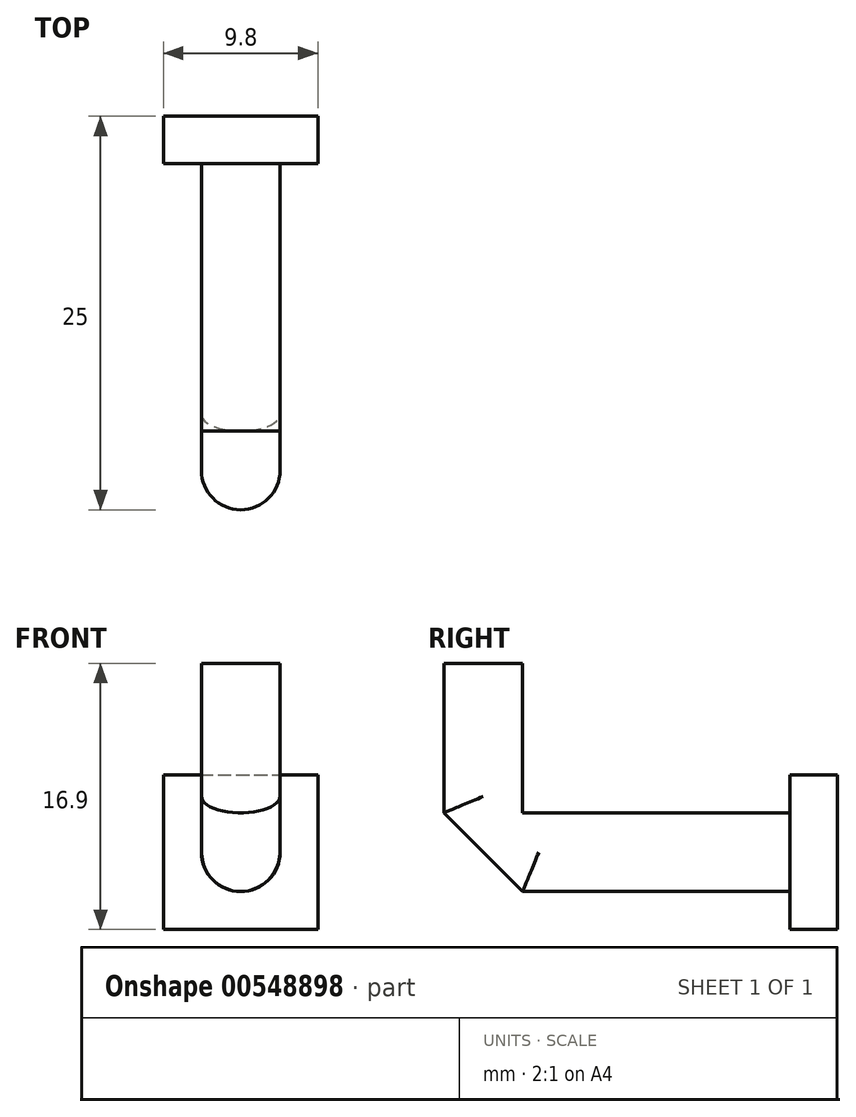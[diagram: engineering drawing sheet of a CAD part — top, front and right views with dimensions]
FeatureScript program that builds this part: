
annotation { "Feature Type Name" : "Feature", "Feature Type Description" : "" }
export const myFeature = defineFeature(function(context is Context, id is Id, definition is map)
    precondition{}
    {
        {
            var Q0;
            Q0=qCreatedBy(makeId("Front.planeOp"),FACE);
            var sketch = newSketch(context, id + "F0", { "sketchPlane" : qUnion([Q0])});
            skLineSegment(sketch, "E0.bottom", {"start": v(-4.9, 4.9) * mm, "end": v(4.9, 4.9) * mm});
            skLineSegment(sketch, "E0.top", {"start": v(-4.9, -4.9) * mm, "end": v(4.9, -4.9) * mm});
            skLineSegment(sketch, "E0.left", {"start": v(-4.9, 4.9) * mm, "end": v(-4.9, -4.9) * mm});
            skLineSegment(sketch, "E0.right", {"start": v(4.9, 4.9) * mm, "end": v(4.9, -4.9) * mm});
            skPoint(sketch, "E0.middle", {"position": v(0, 0) * mm});
            skSolve(sketch);
        }
        {
            var Q0;
            Q0=qCreatedBy(makeId("Right.planeOp"),FACE);
            var sketch = newSketch(context, id + "F1", { "sketchPlane" : qUnion([Q0])});
            skLineSegment(sketch, "E1.left", {"start": v(-17, 2.5) * mm, "end": v(-17, -2.5) * mm});
            skLineSegment(sketch, "E2.top", {"start": v(-17, 12) * mm, "end": v(-22, 12) * mm});
            skLineSegment(sketch, "E2.left", {"start": v(-17, -2.5) * mm, "end": v(-17, 12) * mm});
            skLineSegment(sketch, "E2.right", {"start": v(-22, 2.5) * mm, "end": v(-22, 12) * mm});
            skLineSegment(sketch, "E3", {"start": v(-17, -2.5) * mm, "end": v(-22, 2.5) * mm});
            skLineSegment(sketch, "E4", {"start": v(0, -2.5) * mm, "end": v(0, 2.5) * mm});
            skLineSegment(sketch, "E5", {"start": v(0, 2.5) * mm, "end": v(-17, 2.5) * mm});
            skLineSegment(sketch, "E6", {"start": v(-17, -2.5) * mm, "end": v(0, -2.5) * mm});
            skSolve(sketch);
        }
        {
            var Q0;
            Q0 = qSketchRegion(id + "F0", true);
            extrude(context, id + "F2", {"entities" : qUnion([Q0]), "oppositeDirection" : true, "depth" : 3 * mm, "offsetDistance" : 25 * mm});
        }
        {
            var Q0;
            Q0=makeQuery(id+"F1.imprint","IMPRINT",FACE,{"disambiguationData":[TD([[makeQuery(id+"F1.imprint","IMPRINT",EDGE,{"derivedFrom":sQuery(id+"F1.wireOp",EDGE,"E4")}),1.0]])]});
            var Q1;
            {var subQ1=sQuery(id+"F1.wireOp",EDGE,"E2.top");Q1=makeQuery(id+"F1.imprint","IMPRINT",FACE,{"disambiguationData":[TD([[makeQuery(id+"F1.imprint","IMPRINT",EDGE,{"derivedFrom":subQ1}),1.0]])]});}
            extrude(context, id + "F3", {"entities" : qUnion([Q0, Q1]), "operationType" : NewBodyOperationType.ADD, "endBound" : BoundingType.SYMMETRIC, "depth" : 5 * mm, "offsetDistance" : 25 * mm});
        }
        {
            var Q0;
            Q0=makeQuery(id+"F3.opExtrude","CAP_EDGE",EDGE,{"disambiguationData":[OSD([sQuery(id+"F1.wireOp",EDGE,"E6")])],"isStart":true});
            var Q1;
            Q1=makeQuery(id+"F3.opExtrude","CAP_EDGE",EDGE,{"disambiguationData":[OSD([sQuery(id+"F1.wireOp",EDGE,"E3")])],"isStart":true});
            var Q2;
            Q2=makeQuery(id+"F3.opExtrude","CAP_EDGE",EDGE,{"disambiguationData":[OSD([sQuery(id+"F1.wireOp",EDGE,"E6")])],"isStart":false});
            var Q3;
            Q3=makeQuery(id+"F3.opExtrude","CAP_EDGE",EDGE,{"disambiguationData":[OSD([sQuery(id+"F1.wireOp",EDGE,"E3")])],"isStart":false});
            var Q4;
            Q4=makeQuery(id+"F3.opExtrude","CAP_EDGE",EDGE,{"disambiguationData":[OSD([sQuery(id+"F1.wireOp",EDGE,"E2.right")])],"isStart":false});
            var Q5;
            Q5=makeQuery(id+"F3.opExtrude","CAP_EDGE",EDGE,{"disambiguationData":[OSD([sQuery(id+"F1.wireOp",EDGE,"E2.right")])],"isStart":true});
            fillet(context, id + "F4", {"entities" : qUnion([Q0, Q1, Q2, Q3, Q4, Q5]), "radius" : 2.5 * mm, "tangentPropagation" : true, "allowEdgeOverflow" : false});
        }
    });
